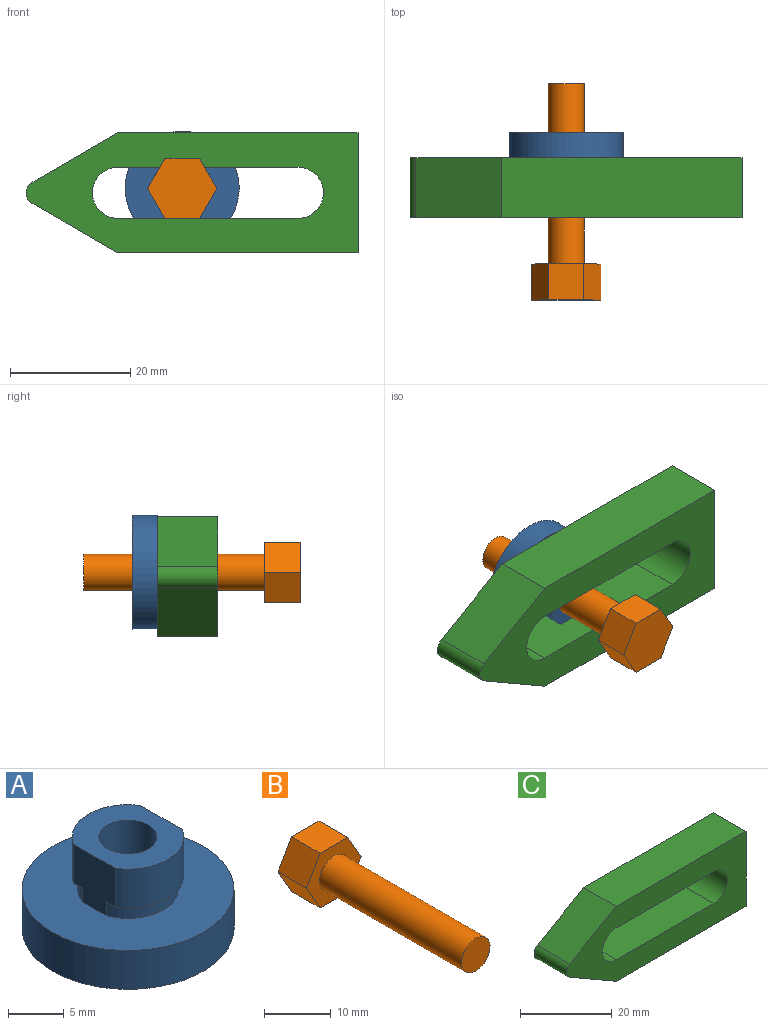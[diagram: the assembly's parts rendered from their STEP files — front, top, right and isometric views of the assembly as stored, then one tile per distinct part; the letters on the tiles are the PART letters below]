
ASSEMBLY  parts=3 mates=3
PART A: 13 faces, bbox 19x19x10 mm
  f0: cylinder r=4.5mm len=8.5mm, axis (0,0,-1), area 16.7mm2, adj f3,f10,f11,f12
  f1: cylinder r=4.5mm len=8.5mm, axis (0,0,-1), area 16.7mm2, adj f2,f10,f11,f12
  f2: plane 8.5x3.52mm, normal (0,0,-1), area 5.3mm2, adj f1,f5,f11,f12
  f3: plane 8.5x3.52mm, normal (0,0,-1), area 5.3mm2, adj f0,f4,f11,f12
  f4: cylinder r=5mm len=8.5mm, axis (0,0,-1), area 43.2mm2, adj f3,f6,f11,f12
  f5: cylinder r=5mm len=8.5mm, axis (0,0,-1), area 43.2mm2, adj f2,f6,f11,f12
  f6: plane 10x8.5mm, normal (0,0,1), area 52mm2, adj f4,f5,f7,f11,f12
  f7: cylinder r=2.6mm len=10mm, axis (0,0,-1), area 163.4mm2, adj f6,f8
  f8: plane 19x19mm, normal (0,0,-1), area 262.3mm2, adj f7,f9
  f9: cylinder r=9.5mm len=19mm, axis (0,0,-1), area 253.7mm2, adj f8,f10
  f10: plane 19x19mm, normal (0,0,1), area 220.9mm2, adj f0,f1,f9,f11,f12
  f11: plane 5.75x5.27mm, normal (1,0,0), area 26.8mm2, adj f0,f1,f2,f3,f4,f5,f6,f10
  f12: plane 5.75x5.27mm, normal (-1,0,0), area 26.8mm2, adj f0,f1,f2,f3,f4,f5,f6,f10
PART B: 10 faces, bbox 11.5x36x10 mm
  f0: cylinder r=3mm len=30mm, axis (0,1,0), area 565.5mm2, adj f1,f9
  f1: plane 6x6mm, normal (0,-1,0), area 28.3mm2, adj f0
  f2: plane 6x5mm, normal (-0.87,0,-0.5), area 34.6mm2, adj f3,f7,f8,f9
  f3: plane 6x5.77mm, normal (0,0,-1), area 34.6mm2, adj f2,f4,f8,f9
  f4: plane 6x5mm, normal (0.87,0,-0.5), area 34.6mm2, adj f3,f5,f8,f9
  f5: plane 6x5mm, normal (0.87,0,0.5), area 34.6mm2, adj f4,f6,f8,f9
  f6: plane 6x5.77mm, normal (0,0,1), area 34.6mm2, adj f5,f7,f8,f9
  f7: plane 6x5mm, normal (-0.87,0,0.5), area 34.6mm2, adj f2,f6,f8,f9
  f8: plane 11.55x10mm, normal (0,1,0), area 86.6mm2, adj f2,f3,f4,f5,f6,f7
  f9: plane 11.55x10mm, normal (0,-1,0), area 58.3mm2, adj f0,f2,f3,f4,f5,f6,f7
PART C: 12 faces, bbox 55.3x10x20 mm
  f0: cylinder r=4.25mm len=10mm, axis (0,1,0), area 133.5mm2, adj f1,f9,f10,f11
  f1: plane 30x10mm, normal (0,0,-1), area 300mm2, adj f0,f2,f10,f11
  f2: cylinder r=4.25mm len=10mm, axis (0,1,0), area 133.5mm2, adj f1,f9,f10,f11
  f3: plane 40x10mm, normal (0,0,-1), area 400mm2, adj f4,f8,f10,f11
  f4: plane 20x10mm, normal (1,0,0), area 200mm2, adj f3,f5,f10,f11
  f5: plane 40x10mm, normal (0,0,1), area 400mm2, adj f4,f6,f10,f11
  f6: plane 14.32x10mm, normal (-0.5,0,0.87), area 165.4mm2, adj f5,f7,f10,f11
  f7: cylinder r=2mm len=10mm, axis (0,1,0), area 41.9mm2, adj f6,f8,f10,f11
  f8: plane 14.32x10mm, normal (-0.5,0,-0.87), area 165.4mm2, adj f3,f7,f10,f11
  f9: plane 30x10mm, normal (0,0,1), area 300mm2, adj f0,f2,f10,f11
  f10: plane 55.32x20mm, normal (0,-1,0), area 658.7mm2, adj f0,f1,f2,f3,f4,f5,f6,f7
  f11: plane 55.32x20mm, normal (0,1,0), area 658.7mm2, adj f0,f1,f2,f3,f4,f5,f6,f7
PLACE A rot(axis=(0.58,0.58,-0.58),120deg) t=(-4.38,13.58,2.81)mm
PLACE B rot(axis=(0,0,1),180deg) t=(-4.38,-8.36,2.81)mm fixed
PLACE C rot(axis=(1,0,0),180deg) t=(-32.4,-0.67,12.03)mm
MATE slider B.f0 <-> A.f0  axis (0,-1,0) through (-4.38,6.64,2.81)mm
MATE planar C.f10 <-> A.f0  axis (0,1,0) through (0.66,9.33,2.03)mm
MATE parallel A.f11 <-> C.f9  axis (0,0,-1) through (-4.38,6.18,-1.44)mm
